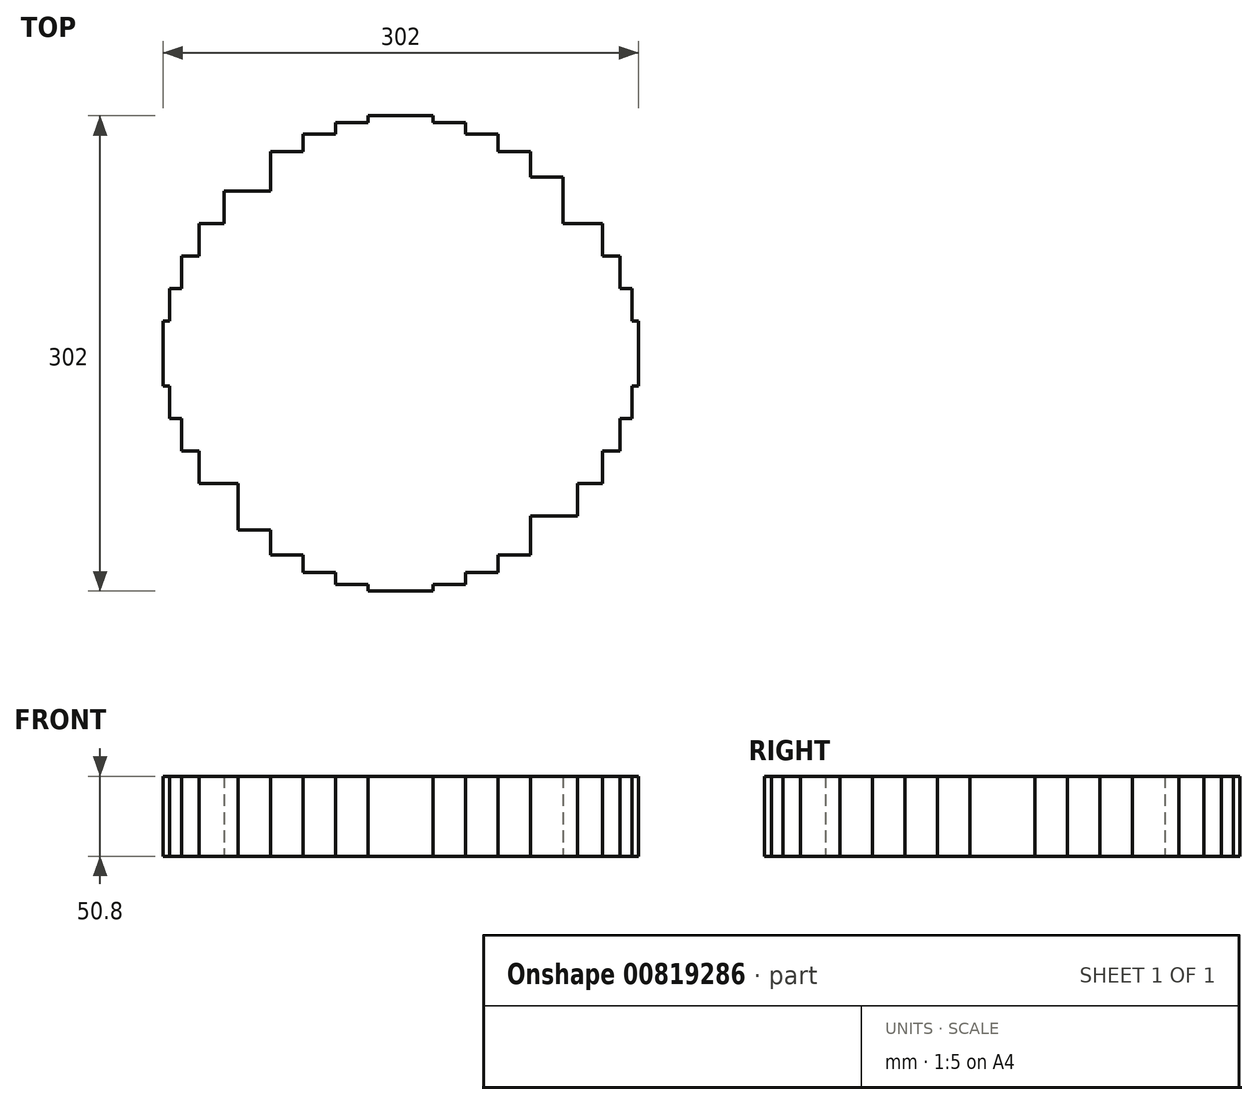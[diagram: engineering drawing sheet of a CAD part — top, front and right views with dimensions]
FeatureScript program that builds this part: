
annotation { "Feature Type Name" : "Feature", "Feature Type Description" : "" }
export const myFeature = defineFeature(function(context is Context, id is Id, definition is map)
    precondition{}
    {
        {
            var Q0;
            Q0=qCreatedBy(makeId("Top.planeOp"),FACE);
            var sketch = newSketch(context, id + "F0", { "sketchPlane" : qUnion([Q0])});
            skCircle(sketch, "E0", {"center": v(0, 0) * mm, "radius": 152.4 * mm, "construction": true});
            skLineSegment(sketch, "E1", {"start": v(0, 152.4) * mm, "end": v(0, -152.4) * mm, "construction": true});
            skLineSegment(sketch, "E2", {"start": v(-152.4, 0) * mm, "end": v(152.4, 0) * mm, "construction": true});
            skLineSegment(sketch, "E3.bottom", {"start": v(0, 0) * mm, "end": v(-20.64, 0) * mm});
            skLineSegment(sketch, "E3.top", {"start": v(0, -151) * mm, "end": v(-20.64, -151) * mm});
            skLineSegment(sketch, "E3.left", {"start": v(0, 0) * mm, "end": v(0, -151) * mm});
            skLineSegment(sketch, "E3.right", {"start": v(-20.64, 0) * mm, "end": v(-20.64, -151) * mm});
            skLineSegment(sketch, "E4.bottom", {"start": v(-20.64, 0) * mm, "end": v(-151, 0) * mm});
            skLineSegment(sketch, "E4.top", {"start": v(-20.64, -20.64) * mm, "end": v(-151, -20.64) * mm});
            skLineSegment(sketch, "E4.left", {"start": v(-20.64, 0) * mm, "end": v(-20.64, -20.64) * mm});
            skLineSegment(sketch, "E4.right", {"start": v(-151, 0) * mm, "end": v(-151, -20.64) * mm});
            skLineSegment(sketch, "E5.bottom", {"start": v(-20.64, -20.64) * mm, "end": v(-41.28, -20.64) * mm});
            skLineSegment(sketch, "E5.top", {"start": v(-20.64, -146.7) * mm, "end": v(-41.27, -146.7) * mm});
            skLineSegment(sketch, "E5.left", {"start": v(-20.64, -20.64) * mm, "end": v(-20.64, -146.7) * mm});
            skLineSegment(sketch, "E5.right", {"start": v(-41.28, -20.64) * mm, "end": v(-41.27, -146.7) * mm});
            skLineSegment(sketch, "E6.bottom", {"start": v(-41.28, -20.64) * mm, "end": v(-146.7, -20.64) * mm});
            skLineSegment(sketch, "E6.top", {"start": v(-41.28, -41.28) * mm, "end": v(-146.7, -41.28) * mm});
            skLineSegment(sketch, "E6.left", {"start": v(-41.28, -20.64) * mm, "end": v(-41.28, -41.28) * mm});
            skLineSegment(sketch, "E6.right", {"start": v(-146.7, -20.64) * mm, "end": v(-146.7, -41.28) * mm});
            skLineSegment(sketch, "E7.bottom", {"start": v(-41.28, -41.28) * mm, "end": v(-61.91, -41.28) * mm});
            skLineSegment(sketch, "E7.top", {"start": v(-41.27, -139.26) * mm, "end": v(-61.91, -139.26) * mm});
            skLineSegment(sketch, "E7.left", {"start": v(-41.28, -41.28) * mm, "end": v(-41.27, -139.26) * mm});
            skLineSegment(sketch, "E7.right", {"start": v(-61.91, -41.28) * mm, "end": v(-61.91, -139.26) * mm});
            skLineSegment(sketch, "E8.bottom", {"start": v(-61.91, -41.28) * mm, "end": v(-139.26, -41.28) * mm});
            skLineSegment(sketch, "E8.top", {"start": v(-61.91, -61.91) * mm, "end": v(-139.26, -61.91) * mm});
            skLineSegment(sketch, "E8.left", {"start": v(-61.91, -41.28) * mm, "end": v(-61.91, -61.91) * mm});
            skLineSegment(sketch, "E8.right", {"start": v(-139.26, -41.28) * mm, "end": v(-139.26, -61.91) * mm});
            skLineSegment(sketch, "E9.bottom", {"start": v(-61.91, -61.91) * mm, "end": v(-82.55, -61.91) * mm});
            skLineSegment(sketch, "E9.top", {"start": v(-61.91, -128.1) * mm, "end": v(-82.55, -128.1) * mm});
            skLineSegment(sketch, "E9.left", {"start": v(-61.91, -61.91) * mm, "end": v(-61.91, -128.1) * mm});
            skLineSegment(sketch, "E9.right", {"start": v(-82.55, -61.91) * mm, "end": v(-82.55, -128.1) * mm});
            skLineSegment(sketch, "E10.bottom", {"start": v(-82.55, -61.91) * mm, "end": v(-128.1, -61.91) * mm});
            skLineSegment(sketch, "E10.top", {"start": v(-82.55, -82.55) * mm, "end": v(-128.1, -82.55) * mm});
            skLineSegment(sketch, "E10.left", {"start": v(-82.55, -61.91) * mm, "end": v(-82.55, -82.55) * mm});
            skLineSegment(sketch, "E10.right", {"start": v(-128.1, -61.91) * mm, "end": v(-128.1, -82.55) * mm});
            skLineSegment(sketch, "E11.bottom", {"start": v(-82.55, -82.55) * mm, "end": v(-103.19, -82.55) * mm});
            skLineSegment(sketch, "E11.top", {"start": v(-82.55, -112.15) * mm, "end": v(-103.19, -112.15) * mm});
            skLineSegment(sketch, "E11.left", {"start": v(-82.55, -82.55) * mm, "end": v(-82.55, -112.15) * mm});
            skLineSegment(sketch, "E11.right", {"start": v(-103.19, -82.55) * mm, "end": v(-103.19, -112.15) * mm});
            skLineSegment(sketch, "E12.1.0", {"start": v(0, 0) * mm, "end": v(151, 0) * mm});
            skLineSegment(sketch, "E12.1.1", {"start": v(82.55, -82.55) * mm, "end": v(112.15, -82.55) * mm});
            skLineSegment(sketch, "E12.1.2", {"start": v(41.28, -41.28) * mm, "end": v(139.26, -41.27) * mm});
            skLineSegment(sketch, "E12.1.3", {"start": v(41.28, -41.28) * mm, "end": v(41.28, -146.7) * mm});
            skLineSegment(sketch, "E12.1.4", {"start": v(0, -20.64) * mm, "end": v(151, -20.64) * mm});
            skLineSegment(sketch, "E12.1.5", {"start": v(0, -20.64) * mm, "end": v(0, -151) * mm});
            skLineSegment(sketch, "E12.1.6", {"start": v(20.64, -20.64) * mm, "end": v(20.64, -151) * mm});
            skLineSegment(sketch, "E12.1.7", {"start": v(82.55, -82.55) * mm, "end": v(82.55, -128.1) * mm});
            skLineSegment(sketch, "E12.1.8", {"start": v(41.28, -61.91) * mm, "end": v(139.26, -61.91) * mm});
            skLineSegment(sketch, "E12.1.9", {"start": v(82.55, -103.19) * mm, "end": v(112.15, -103.19) * mm});
            skLineSegment(sketch, "E12.1.10", {"start": v(61.91, -82.55) * mm, "end": v(61.91, -128.1) * mm});
            skLineSegment(sketch, "E12.1.11", {"start": v(61.91, -82.55) * mm, "end": v(128.1, -82.55) * mm});
            skLineSegment(sketch, "E12.1.12", {"start": v(20.64, -41.28) * mm, "end": v(20.64, -146.7) * mm});
            skLineSegment(sketch, "E12.1.13", {"start": v(41.28, -61.91) * mm, "end": v(41.28, -139.26) * mm});
            skLineSegment(sketch, "E12.1.14", {"start": v(61.91, -61.91) * mm, "end": v(61.91, -139.26) * mm});
            skLineSegment(sketch, "E12.1.15", {"start": v(20.64, -41.28) * mm, "end": v(146.7, -41.27) * mm});
            skLineSegment(sketch, "E12.1.16", {"start": v(61.91, -61.91) * mm, "end": v(128.1, -61.91) * mm});
            skLineSegment(sketch, "E12.1.17", {"start": v(20.64, -20.64) * mm, "end": v(146.7, -20.64) * mm});
            skLineSegment(sketch, "E12.1.18", {"start": v(151, 0) * mm, "end": v(151, -20.64) * mm});
            skLineSegment(sketch, "E12.1.19", {"start": v(128.1, -61.91) * mm, "end": v(128.1, -82.55) * mm});
            skLineSegment(sketch, "E12.1.20", {"start": v(139.26, -41.27) * mm, "end": v(139.26, -61.91) * mm});
            skLineSegment(sketch, "E12.1.21", {"start": v(146.7, -20.64) * mm, "end": v(146.7, -41.27) * mm});
            skLineSegment(sketch, "E12.1.22", {"start": v(112.15, -82.55) * mm, "end": v(112.15, -103.19) * mm});
            skLineSegment(sketch, "E12.1.23", {"start": v(0, -151) * mm, "end": v(20.64, -151) * mm});
            skLineSegment(sketch, "E12.1.24", {"start": v(82.55, -82.55) * mm, "end": v(82.55, -103.19) * mm});
            skLineSegment(sketch, "E12.1.25", {"start": v(41.28, -139.26) * mm, "end": v(61.91, -139.26) * mm});
            skLineSegment(sketch, "E12.1.26", {"start": v(20.64, -146.7) * mm, "end": v(41.28, -146.7) * mm});
            skLineSegment(sketch, "E12.1.27", {"start": v(61.91, -128.1) * mm, "end": v(82.55, -128.1) * mm});
            skLineSegment(sketch, "E12.1.28", {"start": v(0, 0) * mm, "end": v(0, -20.64) * mm});
            skLineSegment(sketch, "E12.1.29", {"start": v(20.64, -41.28) * mm, "end": v(41.28, -41.28) * mm});
            skLineSegment(sketch, "E12.1.30", {"start": v(61.91, -82.55) * mm, "end": v(82.55, -82.55) * mm});
            skLineSegment(sketch, "E12.1.31", {"start": v(61.91, -61.91) * mm, "end": v(61.91, -82.55) * mm});
            skLineSegment(sketch, "E12.1.32", {"start": v(0, -20.64) * mm, "end": v(20.64, -20.64) * mm});
            skLineSegment(sketch, "E12.1.33", {"start": v(20.64, -20.64) * mm, "end": v(20.64, -41.28) * mm});
            skLineSegment(sketch, "E12.1.34", {"start": v(41.28, -41.28) * mm, "end": v(41.28, -61.91) * mm});
            skLineSegment(sketch, "E12.1.35", {"start": v(41.28, -61.91) * mm, "end": v(61.91, -61.91) * mm});
            skLineSegment(sketch, "E12.2.0", {"start": v(0, 0) * mm, "end": v(0, 151) * mm});
            skLineSegment(sketch, "E12.2.1", {"start": v(82.55, 82.55) * mm, "end": v(82.55, 112.15) * mm});
            skLineSegment(sketch, "E12.2.2", {"start": v(41.28, 41.28) * mm, "end": v(41.28, 139.26) * mm});
            skLineSegment(sketch, "E12.2.3", {"start": v(41.28, 41.28) * mm, "end": v(146.7, 41.28) * mm});
            skLineSegment(sketch, "E12.2.4", {"start": v(20.64, 0) * mm, "end": v(20.64, 151) * mm});
            skLineSegment(sketch, "E12.2.5", {"start": v(20.64, 0) * mm, "end": v(151, 0) * mm});
            skLineSegment(sketch, "E12.2.6", {"start": v(20.64, 20.64) * mm, "end": v(151, 20.64) * mm});
            skLineSegment(sketch, "E12.2.7", {"start": v(82.55, 82.55) * mm, "end": v(128.1, 82.55) * mm});
            skLineSegment(sketch, "E12.2.8", {"start": v(61.91, 41.28) * mm, "end": v(61.91, 139.26) * mm});
            skLineSegment(sketch, "E12.2.9", {"start": v(103.19, 82.55) * mm, "end": v(103.19, 112.15) * mm});
            skLineSegment(sketch, "E12.2.10", {"start": v(82.55, 61.91) * mm, "end": v(128.1, 61.91) * mm});
            skLineSegment(sketch, "E12.2.11", {"start": v(82.55, 61.91) * mm, "end": v(82.55, 128.1) * mm});
            skLineSegment(sketch, "E12.2.12", {"start": v(41.28, 20.64) * mm, "end": v(146.7, 20.64) * mm});
            skLineSegment(sketch, "E12.2.13", {"start": v(61.91, 41.28) * mm, "end": v(139.26, 41.28) * mm});
            skLineSegment(sketch, "E12.2.14", {"start": v(61.91, 61.91) * mm, "end": v(139.26, 61.91) * mm});
            skLineSegment(sketch, "E12.2.15", {"start": v(41.28, 20.64) * mm, "end": v(41.27, 146.7) * mm});
            skLineSegment(sketch, "E12.2.16", {"start": v(61.91, 61.91) * mm, "end": v(61.91, 128.1) * mm});
            skLineSegment(sketch, "E12.2.17", {"start": v(20.64, 20.64) * mm, "end": v(20.64, 146.7) * mm});
            skLineSegment(sketch, "E12.2.18", {"start": v(0, 151) * mm, "end": v(20.64, 151) * mm});
            skLineSegment(sketch, "E12.2.19", {"start": v(61.91, 128.1) * mm, "end": v(82.55, 128.1) * mm});
            skLineSegment(sketch, "E12.2.20", {"start": v(41.27, 139.26) * mm, "end": v(61.91, 139.26) * mm});
            skLineSegment(sketch, "E12.2.21", {"start": v(20.64, 146.7) * mm, "end": v(41.28, 146.7) * mm});
            skLineSegment(sketch, "E12.2.22", {"start": v(82.55, 112.15) * mm, "end": v(103.19, 112.15) * mm});
            skLineSegment(sketch, "E12.2.23", {"start": v(151, 0) * mm, "end": v(151, 20.64) * mm});
            skLineSegment(sketch, "E12.2.24", {"start": v(82.55, 82.55) * mm, "end": v(103.19, 82.55) * mm});
            skLineSegment(sketch, "E12.2.25", {"start": v(139.26, 41.28) * mm, "end": v(139.26, 61.91) * mm});
            skLineSegment(sketch, "E12.2.26", {"start": v(146.7, 20.64) * mm, "end": v(146.7, 41.28) * mm});
            skLineSegment(sketch, "E12.2.27", {"start": v(128.1, 61.91) * mm, "end": v(128.1, 82.55) * mm});
            skLineSegment(sketch, "E12.2.28", {"start": v(0, 0) * mm, "end": v(20.64, 0) * mm});
            skLineSegment(sketch, "E12.2.29", {"start": v(41.28, 20.64) * mm, "end": v(41.28, 41.28) * mm});
            skLineSegment(sketch, "E12.2.30", {"start": v(82.55, 61.91) * mm, "end": v(82.55, 82.55) * mm});
            skLineSegment(sketch, "E12.2.31", {"start": v(61.91, 61.91) * mm, "end": v(82.55, 61.91) * mm});
            skLineSegment(sketch, "E12.2.32", {"start": v(20.64, 0) * mm, "end": v(20.64, 20.64) * mm});
            skLineSegment(sketch, "E12.2.33", {"start": v(20.64, 20.64) * mm, "end": v(41.28, 20.64) * mm});
            skLineSegment(sketch, "E12.2.34", {"start": v(41.28, 41.28) * mm, "end": v(61.91, 41.28) * mm});
            skLineSegment(sketch, "E12.2.35", {"start": v(61.91, 41.28) * mm, "end": v(61.91, 61.91) * mm});
            skLineSegment(sketch, "E12.3.0", {"start": v(0, 0) * mm, "end": v(-151, 0) * mm});
            skLineSegment(sketch, "E12.3.1", {"start": v(-82.55, 82.55) * mm, "end": v(-112.15, 82.55) * mm});
            skLineSegment(sketch, "E12.3.2", {"start": v(-41.27, 41.28) * mm, "end": v(-139.26, 41.28) * mm});
            skLineSegment(sketch, "E12.3.3", {"start": v(-41.28, 41.28) * mm, "end": v(-41.28, 146.7) * mm});
            skLineSegment(sketch, "E12.3.4", {"start": v(0, 20.64) * mm, "end": v(-151, 20.64) * mm});
            skLineSegment(sketch, "E12.3.5", {"start": v(0, 20.64) * mm, "end": v(0, 151) * mm});
            skLineSegment(sketch, "E12.3.6", {"start": v(-20.64, 20.64) * mm, "end": v(-20.64, 151) * mm});
            skLineSegment(sketch, "E12.3.7", {"start": v(-82.55, 82.55) * mm, "end": v(-82.55, 128.1) * mm});
            skLineSegment(sketch, "E12.3.8", {"start": v(-41.28, 61.91) * mm, "end": v(-139.26, 61.91) * mm});
            skLineSegment(sketch, "E12.3.9", {"start": v(-82.55, 103.19) * mm, "end": v(-112.15, 103.19) * mm});
            skLineSegment(sketch, "E12.3.10", {"start": v(-61.91, 82.55) * mm, "end": v(-61.91, 128.1) * mm});
            skLineSegment(sketch, "E12.3.11", {"start": v(-61.91, 82.55) * mm, "end": v(-128.1, 82.55) * mm});
            skLineSegment(sketch, "E12.3.12", {"start": v(-20.64, 41.28) * mm, "end": v(-20.64, 146.7) * mm});
            skLineSegment(sketch, "E12.3.13", {"start": v(-41.28, 61.91) * mm, "end": v(-41.28, 139.26) * mm});
            skLineSegment(sketch, "E12.3.14", {"start": v(-61.91, 61.91) * mm, "end": v(-61.91, 139.26) * mm});
            skLineSegment(sketch, "E12.3.15", {"start": v(-20.64, 41.28) * mm, "end": v(-146.7, 41.28) * mm});
            skLineSegment(sketch, "E12.3.16", {"start": v(-61.91, 61.91) * mm, "end": v(-128.1, 61.91) * mm});
            skLineSegment(sketch, "E12.3.17", {"start": v(-20.64, 20.64) * mm, "end": v(-146.7, 20.64) * mm});
            skLineSegment(sketch, "E12.3.18", {"start": v(-151, 0) * mm, "end": v(-151, 20.64) * mm});
            skLineSegment(sketch, "E12.3.19", {"start": v(-128.1, 61.91) * mm, "end": v(-128.1, 82.55) * mm});
            skLineSegment(sketch, "E12.3.20", {"start": v(-139.26, 41.28) * mm, "end": v(-139.26, 61.91) * mm});
            skLineSegment(sketch, "E12.3.21", {"start": v(-146.7, 20.64) * mm, "end": v(-146.7, 41.28) * mm});
            skLineSegment(sketch, "E12.3.22", {"start": v(-112.15, 82.55) * mm, "end": v(-112.15, 103.19) * mm});
            skLineSegment(sketch, "E12.3.23", {"start": v(0, 151) * mm, "end": v(-20.64, 151) * mm});
            skLineSegment(sketch, "E12.3.24", {"start": v(-82.55, 82.55) * mm, "end": v(-82.55, 103.19) * mm});
            skLineSegment(sketch, "E12.3.25", {"start": v(-41.28, 139.26) * mm, "end": v(-61.91, 139.26) * mm});
            skLineSegment(sketch, "E12.3.26", {"start": v(-20.64, 146.7) * mm, "end": v(-41.28, 146.7) * mm});
            skLineSegment(sketch, "E12.3.27", {"start": v(-61.91, 128.1) * mm, "end": v(-82.55, 128.1) * mm});
            skLineSegment(sketch, "E12.3.28", {"start": v(0, 0) * mm, "end": v(0, 20.64) * mm});
            skLineSegment(sketch, "E12.3.29", {"start": v(-20.64, 41.28) * mm, "end": v(-41.28, 41.28) * mm});
            skLineSegment(sketch, "E12.3.30", {"start": v(-61.91, 82.55) * mm, "end": v(-82.55, 82.55) * mm});
            skLineSegment(sketch, "E12.3.31", {"start": v(-61.91, 61.91) * mm, "end": v(-61.91, 82.55) * mm});
            skLineSegment(sketch, "E12.3.32", {"start": v(0, 20.64) * mm, "end": v(-20.64, 20.64) * mm});
            skLineSegment(sketch, "E12.3.33", {"start": v(-20.64, 20.64) * mm, "end": v(-20.64, 41.28) * mm});
            skLineSegment(sketch, "E12.3.34", {"start": v(-41.28, 41.28) * mm, "end": v(-41.28, 61.91) * mm});
            skLineSegment(sketch, "E12.3.35", {"start": v(-41.28, 61.91) * mm, "end": v(-61.91, 61.91) * mm});
            skSolve(sketch);
        }
        {
            var Q0;
            Q0 = qSketchRegion(id + "F0", true);
            extrude(context, id + "F1", {"entities" : qUnion([Q0]), "depth" : 50.8 * mm, "offsetDistance" : 25.4 * mm});
        }
    });
